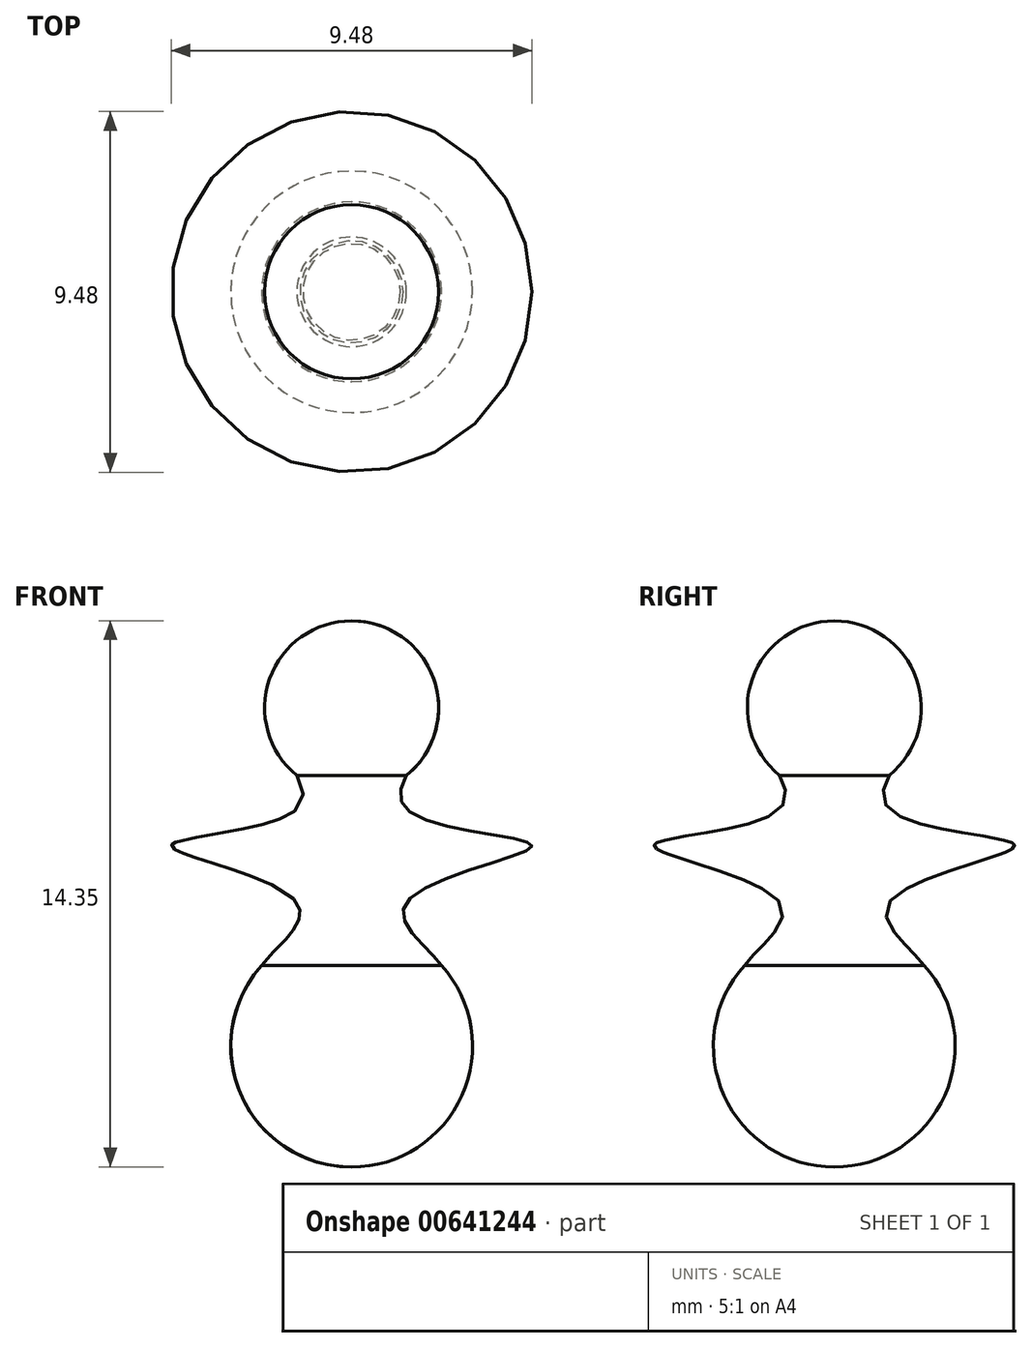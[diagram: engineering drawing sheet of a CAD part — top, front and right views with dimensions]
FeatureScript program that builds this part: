
annotation { "Feature Type Name" : "Feature", "Feature Type Description" : "" }
export const myFeature = defineFeature(function(context is Context, id is Id, definition is map)
    precondition{}
    {
        {
            var Q0;
            Q0=qCreatedBy(makeId("Front.planeOp"),FACE);
            var sketch = newSketch(context, id + "F0", { "sketchPlane" : qUnion([Q0])});
            skArc(sketch, "E0", {"start": v(0, -3.18) * mm, "mid": v(2.9, -1.3) * mm, "end": v(2.36, 2.12) * mm});
            skLineSegment(sketch, "E1", {"start": v(-2.2, 8.26) * mm, "end": v(-2.2, 8.26) * mm});
            skFitSpline(sketch, "E2", {"points": [v(2.2, 8.26) * mm, v(1.37, 6.3) * mm, v(4.74, 5.27) * mm, v(1.4, 3.73) * mm, v(2.36, 2.12) * mm], "startDerivative": vector(-3.35, -7.09) * mm, "endDerivative": vector(4.16, -6.19) * mm});
            skLineSegment(sketch, "E3", {"start": v(0, 11.18) * mm, "end": v(0, -3.17) * mm});
            skArc(sketch, "E4.trimOffspring", {"start": v(1.44, 7.11) * mm, "mid": v(2.15, 9.65) * mm, "end": v(0, 11.18) * mm});
            skPoint(sketch, "E5.MirrorCS.end.orphan", {"position": v(-2.36, 2.12) * mm});
            skSolve(sketch);
        }
        {
            var Q0;
            Q0 = qSketchRegion(id + "F0", true);
            var Q1;
            Q1=sQuery(id+"F0.wireOp",EDGE,"E3");
            revolve(context, id + "F1", {"entities" : qUnion([Q0]), "axis" : qUnion([Q1]), "revolveType" : RevolveType.FULL});
        }
    });
